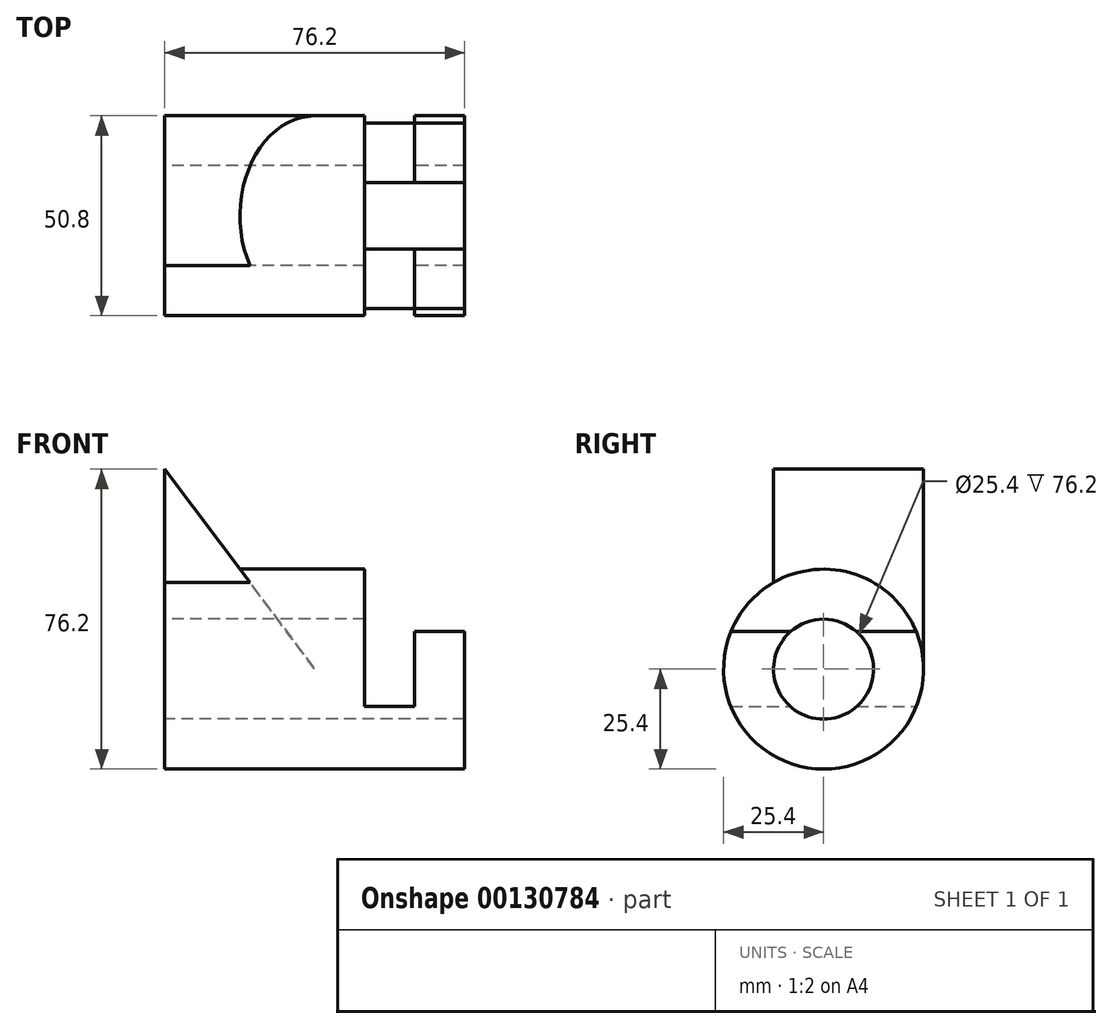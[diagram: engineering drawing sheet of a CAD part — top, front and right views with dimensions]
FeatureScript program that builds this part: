
annotation { "Feature Type Name" : "Feature", "Feature Type Description" : "" }
export const myFeature = defineFeature(function(context is Context, id is Id, definition is map)
    precondition{}
    {
        {
            var Q0;
            Q0=qCreatedBy(makeId("Right.planeOp"),FACE);
            var sketch = newSketch(context, id + "F0", { "sketchPlane" : qUnion([Q0])});
            skCircle(sketch, "E0", {"center": v(0, 0) * mm, "radius": 12.7 * mm});
            skCircle(sketch, "E1", {"center": v(0, 0) * mm, "radius": 25.4 * mm});
            skSolve(sketch);
        }
        {
            var Q0;
            Q0 = qSketchRegion(id + "F0", true);
            extrude(context, id + "F1", {"entities" : qUnion([Q0]), "depth" : 76.2 * mm});
        }
        {
            var Q0;
            Q0=qCreatedBy(makeId("Front.planeOp"),FACE);
            var sketch = newSketch(context, id + "F2", { "sketchPlane" : qUnion([Q0])});
            skLineSegment(sketch, "E2", {"start": v(76.2, 25.4) * mm, "end": v(50.8, 25.4) * mm});
            skLineSegment(sketch, "E3", {"start": v(50.8, 25.4) * mm, "end": v(50.8, -9.52) * mm});
            skLineSegment(sketch, "E4", {"start": v(50.8, -9.52) * mm, "end": v(63.5, -9.52) * mm});
            skLineSegment(sketch, "E5", {"start": v(63.5, -9.52) * mm, "end": v(63.5, 9.53) * mm});
            skLineSegment(sketch, "E6", {"start": v(63.5, 9.53) * mm, "end": v(76.2, 9.53) * mm});
            skLineSegment(sketch, "E7", {"start": v(76.2, 9.53) * mm, "end": v(76.2, 25.4) * mm});
            skSolve(sketch);
        }
        {
            var Q0;
            Q0 = qSketchRegion(id + "F2", true);
            extrude(context, id + "F3", {"entities" : qUnion([Q0]), "operationType" : NewBodyOperationType.REMOVE, "endBound" : BoundingType.SYMMETRIC, "depth" : 50.8 * mm});
        }
        {
            var Q0;
            Q0=qCreatedBy(makeId("Front.planeOp"),FACE);
            var sketch = newSketch(context, id + "F4", { "sketchPlane" : qUnion([Q0])});
            skLineSegment(sketch, "E8", {"start": v(0, 0) * mm, "end": v(0, 50.8) * mm});
            skLineSegment(sketch, "E9", {"start": v(0, 50.8) * mm, "end": v(38.1, 0) * mm});
            skLineSegment(sketch, "E10", {"start": v(38.1, 0) * mm, "end": v(0, 0) * mm});
            skSolve(sketch);
        }
        {
            var Q0;
            Q0 = qSketchRegion(id + "F4", true);
            extrude(context, id + "F5", {"entities" : qUnion([Q0]), "operationType" : NewBodyOperationType.ADD, "depth" : 12.7 * mm, "hasSecondDirection" : true, "secondDirectionOppositeDirection" : true, "secondDirectionDepth" : 25.4 * mm});
        }
        {
            var Q0;
            Q0=qCreatedBy(makeId("Right.planeOp"),FACE);
            var sketch = newSketch(context, id + "F6", { "sketchPlane" : qUnion([Q0])});
            skCircle(sketch, "E11", {"center": v(0, 0) * mm, "radius": 12.7 * mm});
            skSolve(sketch);
        }
        {
            var Q0;
            Q0 = qSketchRegion(id + "F6", true);
            extrude(context, id + "F7", {"entities" : qUnion([Q0]), "operationType" : NewBodyOperationType.REMOVE, "depth" : 38.1 * mm});
        }
    });
